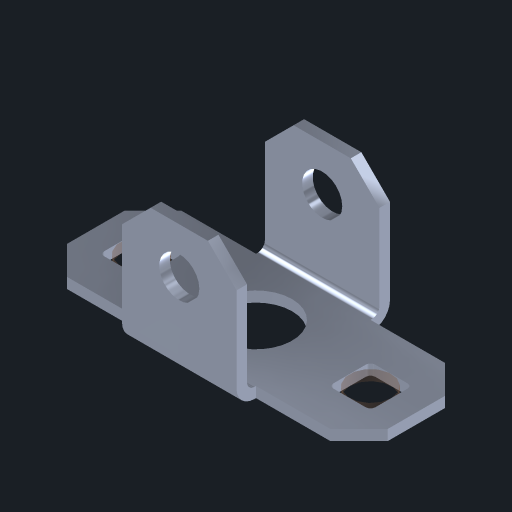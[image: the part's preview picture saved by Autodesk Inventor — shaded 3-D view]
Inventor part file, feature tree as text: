
AUTODESK INVENTOR PART (.ipt)
format: ipt  version: 2023 (Build 270158030, 158C)  size: 207,360 bytes
history: native  units: in
note: dims shown in document units (in); Inventor stores cm internally (conversion verified against a paired STEP export)
features: other x3, extrude x2, chamfer x1, sketch x1, imported_body x1
ambient origin geometry x8: Origin, YZ Plane, XZ Plane, XY Plane, X Axis, Y Axis, Z Axis, Center Point
bodies: Body1 (feature_tree), Body2 (feature_tree), Body3 (feature_tree)
feature tree (8):
  chamfer  "Chamfer1"  Distance=1.0in
  other  "VL-PNEU-PVT-0011"
  sketch  "Sketch1"  dims[d2=1.0in d3=0.0in]
  imported_body  "Base1"
  other  "Srf1"
  other  "Srf2"
  extrude  "ExtrusionSrf1"  [1 undecoded]
  extrude  "ExtrusionSrf2"  [1 undecoded]
note: 2 required parameter values undecoded (feature->parameter linkage not recoverable at this tier; creation-order binding heuristic only, values carry confidence <= 0.55)
